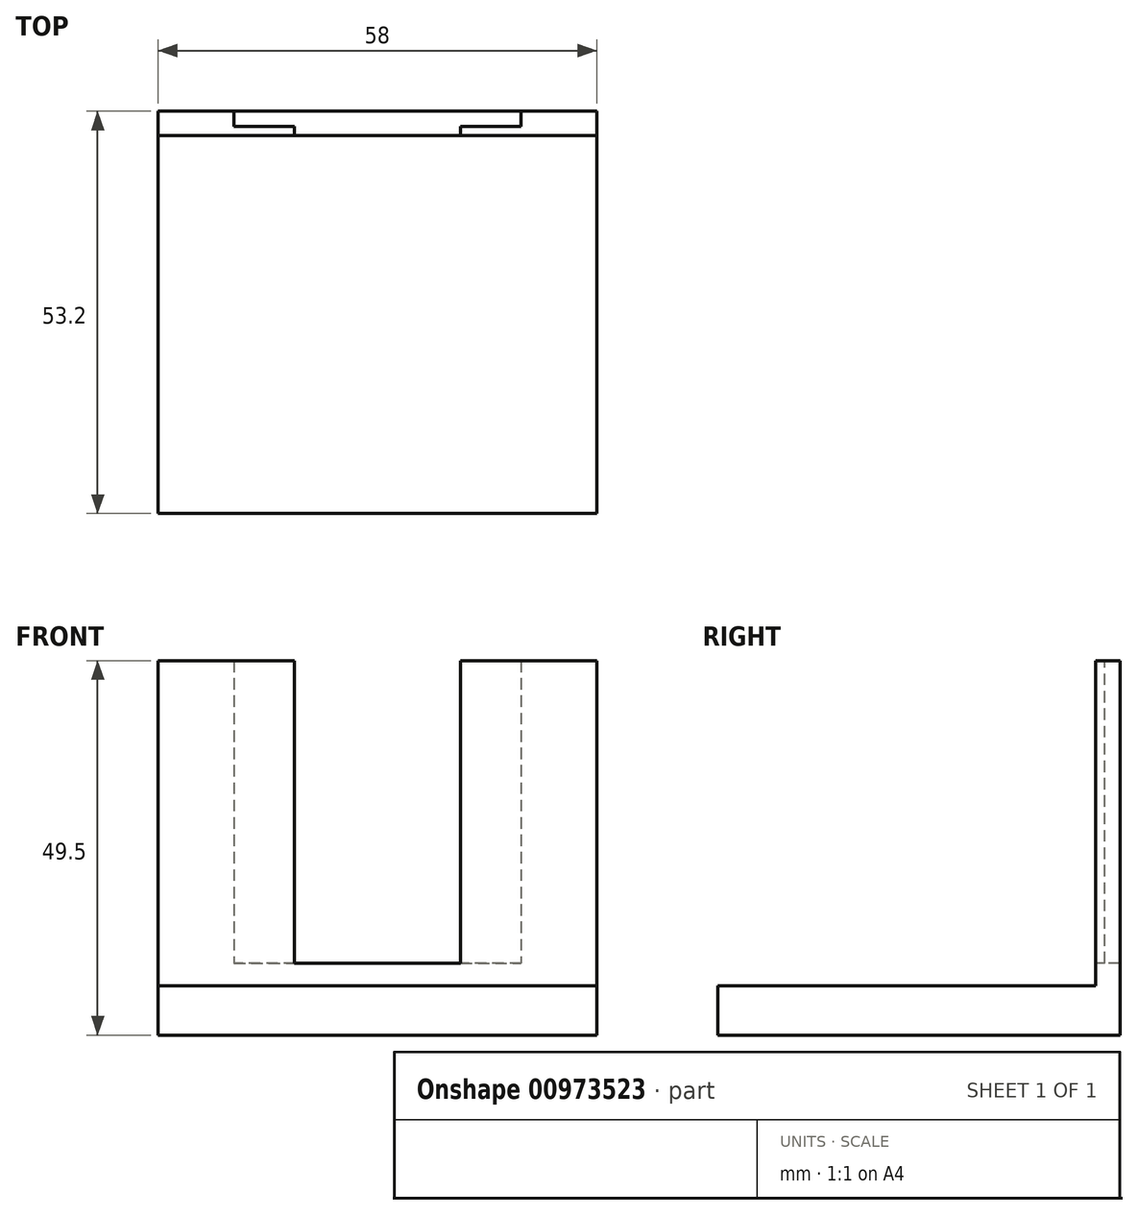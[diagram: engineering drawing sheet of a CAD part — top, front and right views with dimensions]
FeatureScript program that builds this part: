
annotation { "Feature Type Name" : "Feature", "Feature Type Description" : "" }
export const myFeature = defineFeature(function(context is Context, id is Id, definition is map)
    precondition{}
    {
        {
            var Q0;
            Q0=qCreatedBy(makeId("Top.planeOp"),FACE);
            var sketch = newSketch(context, id + "F0", { "sketchPlane" : qUnion([Q0])});
            skLineSegment(sketch, "E0.bottom", {"start": v(0, 0) * mm, "end": v(38, 0) * mm});
            skLineSegment(sketch, "E0.top", {"start": v(0, 1.2) * mm, "end": v(38, 1.2) * mm});
            skLineSegment(sketch, "E0.left", {"start": v(0, 0) * mm, "end": v(0, 1.2) * mm});
            skLineSegment(sketch, "E0.right", {"start": v(38, 0) * mm, "end": v(38, 1.2) * mm});
            skSolve(sketch);
        }
        {
            var Q0;
            Q0=qSketchRegion(id+"F0",true);
            extrude(context, id + "F1", {"entities" : qUnion([Q0]), "depth" : 20 * mm, "offsetDistance" : 25 * mm});
        }
        {
            var Q0;
            Q0=makeQuery(id+"F1.opExtrude","CAP_FACE",FACE,{"disambiguationData":[OSD([sQuery(id+"F0.wireOp",EDGE,"E0.bottom"),sQuery(id+"F0.wireOp",EDGE,"E0.top"),sQuery(id+"F0.wireOp",EDGE,"E0.left"),sQuery(id+"F0.wireOp",EDGE,"E0.right")])],"isStart":false});
            var sketch = newSketch(context, id + "F2", { "sketchPlane" : qUnion([Q0])});
            skLineSegment(sketch, "E1", {"start": v(8, 1.2) * mm, "end": v(8, 0) * mm});
            skLineSegment(sketch, "E2", {"start": v(30, 1.2) * mm, "end": v(30, 0) * mm});
            skLineSegment(sketch, "E3", {"start": v(8, 0) * mm, "end": v(30, 0) * mm});
            skLineSegment(sketch, "E4", {"start": v(30, 1.2) * mm, "end": v(8, 1.2) * mm});
            skSolve(sketch);
        }
        {
            var Q0;
            {var subQ1=sQuery(id+"F0.wireOp",EDGE,"E0.left");var subQ3=sQuery(id+"F0.wireOp",EDGE,"E0.bottom");Q0=makeQuery(id+"F7oCdRpcySzvxNv_1.boolean.opBoolean","SPLIT",FACE,{"disambiguationData":[TD([makeQuery(id+"F1.opExtrude","SWEPT_FACE",FACE,{"disambiguationData":[OSD([subQ1])]})])],"derivedFrom":makeQuery(id+"F1.opExtrude","SWEPT_FACE",FACE,{"disambiguationData":[OSD([subQ3])]})});}
            var sketch = newSketch(context, id + "F3", { "sketchPlane" : qUnion([Q0])});
            skLineSegment(sketch, "E5.bottom", {"start": v(0, 0) * mm, "end": v(-10, 0) * mm});
            skLineSegment(sketch, "E5.top", {"start": v(0, 20) * mm, "end": v(-10, 20) * mm});
            skLineSegment(sketch, "E5.left", {"start": v(0, 0) * mm, "end": v(0, 20) * mm});
            skLineSegment(sketch, "E5.right", {"start": v(-10, 0) * mm, "end": v(-10, 20) * mm});
            skSolve(sketch);
        }
        {
            var Q0;
            Q0=makeQuery(id+"F3.imprint","IMPRINT",FACE,{"disambiguationData":[TD([[makeQuery(id+"F3.imprint","IMPRINT",EDGE,{"derivedFrom":sQuery(id+"F3.wireOp",EDGE,"E5.bottom")}),-1.0]])]});
            extrude(context, id + "F4", {"entities" : qUnion([Q0]), "operationType" : NewBodyOperationType.ADD, "oppositeDirection" : true, "depth" : 3.2 * mm, "offsetDistance" : 25 * mm});
        }
        {
            var Q0;
            Q0=makeQuery(id+"F4.boolean.opBoolean","MERGE",FACE,{"derivedFrom":[makeQuery(id+"F1.opExtrude","SWEPT_FACE",FACE,{"disambiguationData":[OSD([sQuery(id+"F0.wireOp",EDGE,"E0.bottom")])]}),makeQuery(id+"F4.opExtrude","CAP_FACE",FACE,{"disambiguationData":[OSD([sQuery(id+"F3.wireOp",EDGE,"E5.bottom"),sQuery(id+"F3.wireOp",EDGE,"E5.top"),sQuery(id+"F3.wireOp",EDGE,"E5.left"),sQuery(id+"F3.wireOp",EDGE,"E5.right")])],"isStart":true})]});
            var sketch = newSketch(context, id + "F5", { "sketchPlane" : qUnion([Q0])});
            skLineSegment(sketch, "E6.bottom", {"start": v(38, 0) * mm, "end": v(48, 0) * mm});
            skLineSegment(sketch, "E6.top", {"start": v(38, 20) * mm, "end": v(48, 20) * mm});
            skLineSegment(sketch, "E6.left", {"start": v(38, 0) * mm, "end": v(38, 20) * mm});
            skLineSegment(sketch, "E6.right", {"start": v(48, 0) * mm, "end": v(48, 20) * mm});
            skSolve(sketch);
        }
        {
            var Q0;
            Q0=makeQuery(id+"F5.imprint","IMPRINT",FACE,{"disambiguationData":[TD([[makeQuery(id+"F5.imprint","IMPRINT",EDGE,{"derivedFrom":sQuery(id+"F5.wireOp",EDGE,"E6.bottom")}),1.0]])]});
            extrude(context, id + "F6", {"entities" : qUnion([Q0]), "operationType" : NewBodyOperationType.ADD, "oppositeDirection" : true, "depth" : 3.2 * mm, "offsetDistance" : 25 * mm});
        }
        {
            var Q0;
            Q0=makeQuery(id+"F6.boolean.opBoolean","MERGE",FACE,{"derivedFrom":[makeQuery(id+"F4.boolean.opBoolean","MERGE",FACE,{"derivedFrom":[makeQuery(id+"F1.opExtrude","CAP_FACE",FACE,{"disambiguationData":[OSD([sQuery(id+"F0.wireOp",EDGE,"E0.bottom"),sQuery(id+"F0.wireOp",EDGE,"E0.top"),sQuery(id+"F0.wireOp",EDGE,"E0.left"),sQuery(id+"F0.wireOp",EDGE,"E0.right")])],"isStart":true}),makeQuery(id+"F4.opExtrude","SWEPT_FACE",FACE,{"disambiguationData":[OSD([sQuery(id+"F3.wireOp",EDGE,"E5.bottom")])]})]}),makeQuery(id+"F6.opExtrude","SWEPT_FACE",FACE,{"disambiguationData":[OSD([sQuery(id+"F5.wireOp",EDGE,"E6.bottom")])]})]});
            var sketch = newSketch(context, id + "F7", { "sketchPlane" : qUnion([Q0])});
            skLineSegment(sketch, "E7.bottom", {"start": v(48, 0) * mm, "end": v(-10, 0) * mm});
            skLineSegment(sketch, "E7.top", {"start": v(48, -3.2) * mm, "end": v(-10, -3.2) * mm});
            skLineSegment(sketch, "E7.left", {"start": v(48, 0) * mm, "end": v(48, -3.2) * mm});
            skLineSegment(sketch, "E7.right", {"start": v(-10, 0) * mm, "end": v(-10, -3.2) * mm});
            skSolve(sketch);
        }
        {
            var Q0;
            Q0=makeQuery(id+"F7.imprint","IMPRINT",FACE,{"disambiguationData":[TD([[makeQuery(id+"F7.imprint","IMPRINT",EDGE,{"derivedFrom":makeQuery(id+"F1.opExtrude","CAP_EDGE",EDGE,{"disambiguationData":[OSD([sQuery(id+"F0.wireOp",EDGE,"E0.top")])],"isStart":true})}),-1.0]])]});
            var Q1;
            Q1=makeQuery(id+"F7.imprint","IMPRINT",FACE,{"disambiguationData":[TD([[makeQuery(id+"F7.imprint","IMPRINT",EDGE,{"derivedFrom":sQuery(id+"F7.wireOp",EDGE,"E7.bottom")}),-1.0]])]});
            extrude(context, id + "F8", {"entities" : qUnion([Q0, Q1]), "operationType" : NewBodyOperationType.ADD, "depth" : 10 * mm, "offsetDistance" : 25 * mm});
        }
        {
            var Q0;
            Q0=makeQuery(id+"F2.imprint","IMPRINT",FACE,{"disambiguationData":[TD([[makeQuery(id+"F2.imprint","IMPRINT",EDGE,{"derivedFrom":sQuery(id+"F2.wireOp",EDGE,"E1")}),1.0]])]});
            extrude(context, id + "F9", {"entities" : qUnion([Q0]), "operationType" : NewBodyOperationType.REMOVE, "oppositeDirection" : true, "depth" : 20 * mm, "offsetDistance" : 25 * mm});
        }
        {
            var Q0;
            Q0=makeQuery(id+"F8.boolean.opBoolean","MERGE",FACE,{"derivedFrom":[makeQuery(id+"F6.boolean.opBoolean","MERGE",FACE,{"derivedFrom":[makeQuery(id+"F4.boolean.opBoolean","MERGE",FACE,{"derivedFrom":[makeQuery(id+"F1.opExtrude","SWEPT_FACE",FACE,{"disambiguationData":[OSD([sQuery(id+"F0.wireOp",EDGE,"E0.bottom")])]}),makeQuery(id+"F4.opExtrude","CAP_FACE",FACE,{"disambiguationData":[OSD([sQuery(id+"F3.wireOp",EDGE,"E5.bottom"),sQuery(id+"F3.wireOp",EDGE,"E5.top"),sQuery(id+"F3.wireOp",EDGE,"E5.left"),sQuery(id+"F3.wireOp",EDGE,"E5.right")])],"isStart":true})]}),makeQuery(id+"F6.opExtrude","CAP_FACE",FACE,{"disambiguationData":[OSD([sQuery(id+"F5.wireOp",EDGE,"E6.bottom"),sQuery(id+"F5.wireOp",EDGE,"E6.top"),sQuery(id+"F5.wireOp",EDGE,"E6.left"),sQuery(id+"F5.wireOp",EDGE,"E6.right")])],"isStart":true})]}),makeQuery(id+"F8.opExtrude","SWEPT_FACE",FACE,{"disambiguationData":[OSD([sQuery(id+"F7.wireOp",EDGE,"E7.bottom")])]})]});
            var sketch = newSketch(context, id + "F10", { "sketchPlane" : qUnion([Q0])});
            skLineSegment(sketch, "E8.bottom", {"start": v(-10, -10) * mm, "end": v(8, -10) * mm});
            skLineSegment(sketch, "E8.top", {"start": v(-10, -3) * mm, "end": v(8, -3) * mm});
            skLineSegment(sketch, "E8.left", {"start": v(-10, -10) * mm, "end": v(-10, -3) * mm});
            skLineSegment(sketch, "E8.right", {"start": v(8, -10) * mm, "end": v(8, -3) * mm});
            skSolve(sketch);
        }
        {
            var Q0;
            Q0=makeQuery(id+"F10.imprint","IMPRINT",FACE,{"disambiguationData":[TD([[makeQuery(id+"F10.imprint","IMPRINT",EDGE,{"derivedFrom":sQuery(id+"F10.wireOp",EDGE,"E8.bottom")}),1.0]])]});
            extrude(context, id + "F11", {"entities" : qUnion([Q0]), "operationType" : NewBodyOperationType.ADD, "depth" : 50 * mm, "offsetDistance" : 25 * mm});
        }
        {
            var Q0;
            {var subQ1=sQuery(id+"F0.wireOp",EDGE,"E0.top");var subQ2=sQuery(id+"F5.wireOp",EDGE,"E6.left");var subQ3=sQuery(id+"F5.wireOp",EDGE,"E6.top");var subQ5=sQuery(id+"F0.wireOp",EDGE,"E0.bottom");var subQ8=sQuery(id+"F3.wireOp",EDGE,"E5.top");Q0=makeQuery(id+"F9.boolean.opBoolean","SPLIT",FACE,{"disambiguationData":[TD([makeQuery(id+"F6.opExtrude","SWEPT_FACE",FACE,{"disambiguationData":[OSD([subQ2])]})])],"derivedFrom":makeQuery(id+"F6.boolean.opBoolean","MERGE",FACE,{"derivedFrom":[makeQuery(id+"F4.boolean.opBoolean","MERGE",FACE,{"derivedFrom":[makeQuery(id+"F1.opExtrude","CAP_FACE",FACE,{"disambiguationData":[OSD([subQ5,subQ1,sQuery(id+"F0.wireOp",EDGE,"E0.left"),sQuery(id+"F0.wireOp",EDGE,"E0.right")])],"isStart":false}),makeQuery(id+"F4.opExtrude","SWEPT_FACE",FACE,{"disambiguationData":[OSD([subQ8])]})]}),makeQuery(id+"F6.opExtrude","SWEPT_FACE",FACE,{"disambiguationData":[OSD([subQ3])]})]})});}
            var Q1;
            {var subQ2=sQuery(id+"F5.wireOp",EDGE,"E6.top");var subQ4=sQuery(id+"F0.wireOp",EDGE,"E0.bottom");var subQ6=sQuery(id+"F3.wireOp",EDGE,"E5.left");var subQ7=sQuery(id+"F3.wireOp",EDGE,"E5.top");var subQ9=sQuery(id+"F0.wireOp",EDGE,"E0.top");Q1=makeQuery(id+"F9.boolean.opBoolean","SPLIT",FACE,{"disambiguationData":[TD([makeQuery(id+"F4.opExtrude","SWEPT_FACE",FACE,{"disambiguationData":[OSD([subQ6])]})])],"derivedFrom":makeQuery(id+"F6.boolean.opBoolean","MERGE",FACE,{"derivedFrom":[makeQuery(id+"F4.boolean.opBoolean","MERGE",FACE,{"derivedFrom":[makeQuery(id+"F1.opExtrude","CAP_FACE",FACE,{"disambiguationData":[OSD([subQ4,subQ9,sQuery(id+"F0.wireOp",EDGE,"E0.left"),sQuery(id+"F0.wireOp",EDGE,"E0.right")])],"isStart":false}),makeQuery(id+"F4.opExtrude","SWEPT_FACE",FACE,{"disambiguationData":[OSD([subQ7])]})]}),makeQuery(id+"F6.opExtrude","SWEPT_FACE",FACE,{"disambiguationData":[OSD([subQ2])]})]})});}
            extrude(context, id + "F12", {"entities" : qUnion([Q0, Q1]), "operationType" : NewBodyOperationType.ADD, "depth" : 20 * mm, "offsetDistance" : 25 * mm});
        }
        {
            var Q0;
            Q0=makeQuery(id+"F11.opExtrude","SWEPT_FACE",FACE,{"disambiguationData":[OSD([sQuery(id+"F10.wireOp",EDGE,"E8.right")])]});
            extrude(context, id + "F13", {"entities" : qUnion([Q0]), "operationType" : NewBodyOperationType.ADD, "depth" : 40 * mm, "offsetDistance" : 25 * mm});
        }
        {
            var Q0;
            {var subQ0=sQuery(id+"F10.wireOp",EDGE,"E8.bottom");var subQ1=sQuery(id+"F7.wireOp",EDGE,"E7.bottom");Q0=makeQuery(id+"F13.boolean.opBoolean","MERGE",FACE,{"derivedFrom":[makeQuery(id+"F11.boolean.opBoolean","MERGE",FACE,{"derivedFrom":[makeQuery(id+"F8.opExtrude","CAP_FACE",FACE,{"disambiguationData":[OSD([subQ1,sQuery(id+"F7.wireOp",EDGE,"E7.top"),sQuery(id+"F7.wireOp",EDGE,"E7.left"),sQuery(id+"F7.wireOp",EDGE,"E7.right")])],"isStart":false}),makeQuery(id+"F11.opExtrude","SWEPT_FACE",FACE,{"disambiguationData":[OSD([subQ0])]})]}),makeQuery(id+"F13.opExtrude","SWEPT_FACE",FACE,{"disambiguationData":[OSD([subQ1,subQ0,sQuery(id+"F10.wireOp",EDGE,"E8.right")])]})]});}
            extrude(context, id + "F14", {"entities" : qUnion([Q0]), "operationType" : NewBodyOperationType.REMOVE, "oppositeDirection" : true, "depth" : 0.5 * mm, "offsetDistance" : 25 * mm});
        }
    });
